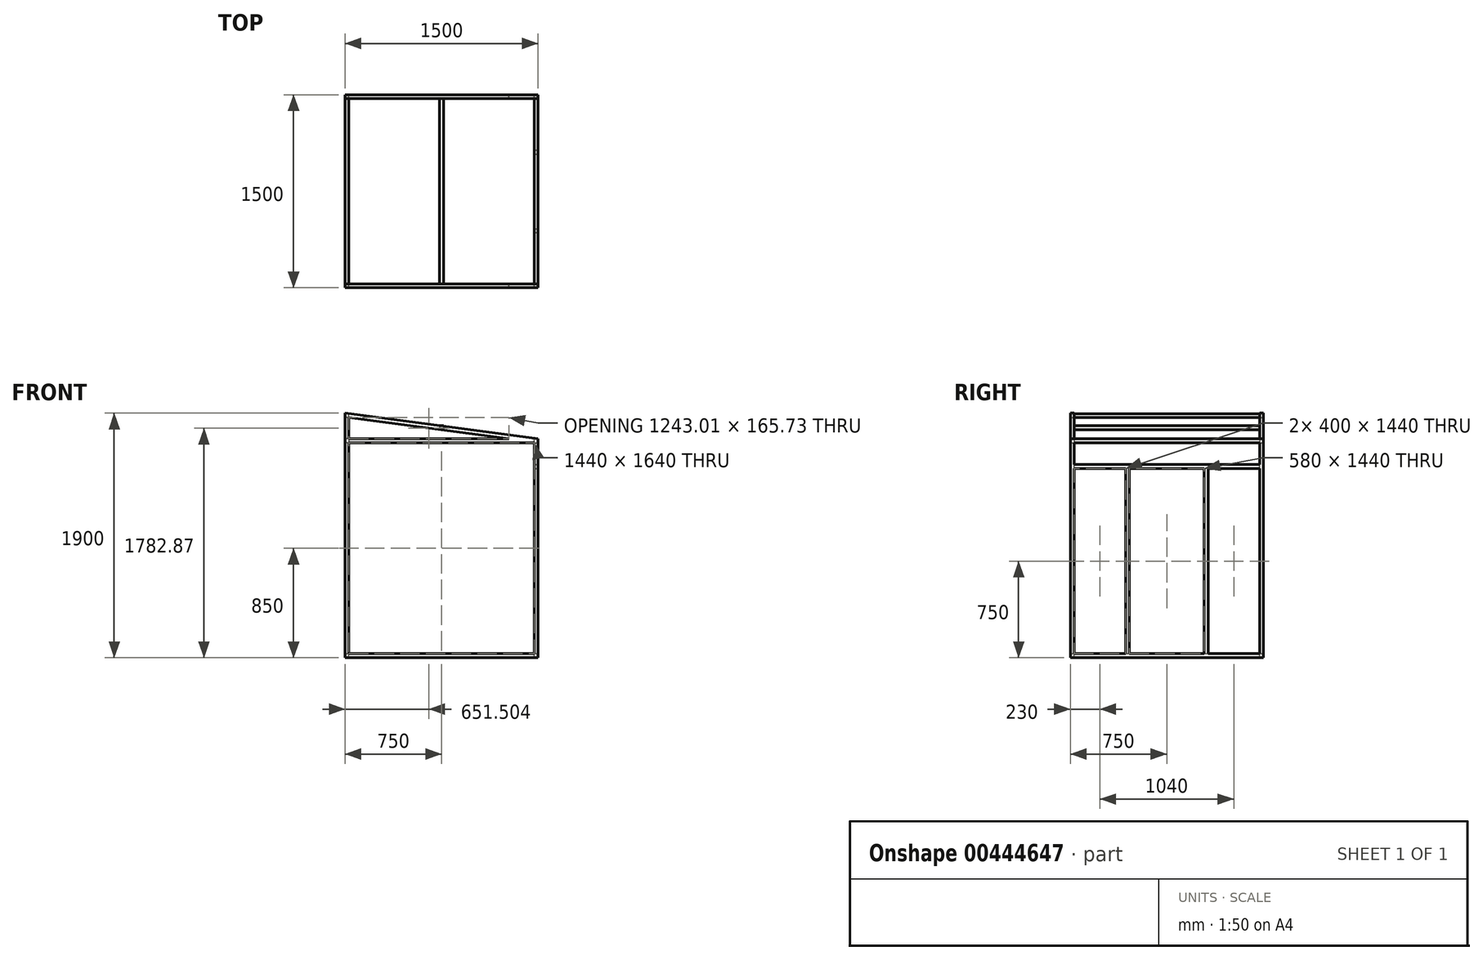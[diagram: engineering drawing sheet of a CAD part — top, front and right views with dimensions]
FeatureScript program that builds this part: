
annotation { "Feature Type Name" : "Feature", "Feature Type Description" : "" }
export const myFeature = defineFeature(function(context is Context, id is Id, definition is map)
    precondition{}
    {
        {
            var Q0;
            Q0=qCreatedBy(makeId("Front.planeOp"),FACE);
            var sketch = newSketch(context, id + "F0", { "sketchPlane" : qUnion([Q0])});
            skLineSegment(sketch, "E0.bottom", {"start": v(0, 0) * mm, "end": v(1500, 0) * mm});
            skLineSegment(sketch, "E0.top", {"start": v(30, 1700) * mm, "end": v(1500, 1700) * mm});
            skLineSegment(sketch, "E0.left", {"start": v(0, 0) * mm, "end": v(0, 1700) * mm});
            skLineSegment(sketch, "E0.right", {"start": v(1500, 0) * mm, "end": v(1500, 1700) * mm});
            skLineSegment(sketch, "E1.0", {"start": v(30, 30) * mm, "end": v(30, 1670) * mm});
            skLineSegment(sketch, "E1.1", {"start": v(30, 30) * mm, "end": v(1470, 30) * mm});
            skLineSegment(sketch, "E1.2", {"start": v(1470, 30) * mm, "end": v(1470, 1670) * mm});
            skLineSegment(sketch, "E1.3", {"start": v(30, 1670) * mm, "end": v(1470, 1670) * mm});
            skLineSegment(sketch, "E2", {"start": v(0, 1700) * mm, "end": v(0, 1900) * mm});
            skLineSegment(sketch, "E3", {"start": v(0, 1900) * mm, "end": v(1500, 1700) * mm});
            skLineSegment(sketch, "E4.0", {"start": v(30, 1865.73) * mm, "end": v(1496.04, 1670.26) * mm});
            skLineSegment(sketch, "E4.1", {"start": v(30, 1500) * mm, "end": v(30, 1865.73) * mm});
            skSolve(sketch);
        }
        {
            var Q0;
            Q0 = qSketchRegion(id + "F0", true);
            extrude(context, id + "F1", {"entities" : qUnion([Q0]), "depth" : 30 * mm});
        }
        {
            var Q0;
            Q0=makeQuery(id+"F1.opExtrude","CAP_FACE",FACE,{"disambiguationData":[OSD([sQuery(id+"F0.wireOp",EDGE,"E0.bottom"),sQuery(id+"F0.wireOp",EDGE,"E0.top"),sQuery(id+"F0.wireOp",EDGE,"E0.left"),sQuery(id+"F0.wireOp",EDGE,"E0.right"),sQuery(id+"F0.wireOp",EDGE,"E1.0"),sQuery(id+"F0.wireOp",EDGE,"E1.1"),sQuery(id+"F0.wireOp",EDGE,"E1.2"),sQuery(id+"F0.wireOp",EDGE,"E1.3")])],"isStart":false});
            var sketch = newSketch(context, id + "F2", { "sketchPlane" : qUnion([Q0])});
            skLineSegment(sketch, "E5.bottom", {"start": v(0, 0) * mm, "end": v(30, 0) * mm});
            skLineSegment(sketch, "E5.top", {"start": v(0, 30) * mm, "end": v(30, 30) * mm});
            skLineSegment(sketch, "E5.left", {"start": v(0, 0) * mm, "end": v(0, 30) * mm});
            skLineSegment(sketch, "E5.right", {"start": v(30, 0) * mm, "end": v(30, 30) * mm});
            skLineSegment(sketch, "E6.bottom", {"start": v(1500, 0) * mm, "end": v(1470, 0) * mm});
            skLineSegment(sketch, "E6.top", {"start": v(1500, 30) * mm, "end": v(1470, 30) * mm});
            skLineSegment(sketch, "E6.left", {"start": v(1500, 0) * mm, "end": v(1500, 30) * mm});
            skLineSegment(sketch, "E6.right", {"start": v(1470, 0) * mm, "end": v(1470, 30) * mm});
            skLineSegment(sketch, "E7.bottom", {"start": v(30, 1700) * mm, "end": v(0, 1700) * mm});
            skLineSegment(sketch, "E7.top", {"start": v(30, 30) * mm, "end": v(0, 30) * mm});
            skLineSegment(sketch, "E8.bottom", {"start": v(1470, 1670) * mm, "end": v(1500, 1670) * mm});
            skLineSegment(sketch, "E8.top", {"start": v(1470, 1700) * mm, "end": v(1500, 1700) * mm});
            skLineSegment(sketch, "E8.left", {"start": v(1470, 1670) * mm, "end": v(1470, 1700) * mm});
            skLineSegment(sketch, "E8.right", {"start": v(1500, 1670) * mm, "end": v(1500, 1700) * mm});
            skLineSegment(sketch, "E9.bottom", {"start": v(30, 1865.73) * mm, "end": v(0, 1865.73) * mm});
            skLineSegment(sketch, "E9.top", {"start": v(30, 1895.73) * mm, "end": v(0, 1895.73) * mm});
            skLineSegment(sketch, "E9.left", {"start": v(30, 1865.73) * mm, "end": v(30, 1895.73) * mm});
            skLineSegment(sketch, "E9.right", {"start": v(0, 1865.73) * mm, "end": v(0, 1895.73) * mm});
            skLineSegment(sketch, "E10.bottom", {"start": v(735, 1802) * mm, "end": v(765, 1802) * mm});
            skLineSegment(sketch, "E10.top", {"start": v(735, 1772) * mm, "end": v(765, 1772) * mm});
            skLineSegment(sketch, "E10.left", {"start": v(735, 1802) * mm, "end": v(735, 1772) * mm});
            skLineSegment(sketch, "E10.right", {"start": v(765, 1802) * mm, "end": v(765, 1772) * mm});
            skLineSegment(sketch, "E11", {"start": v(30, 1670) * mm, "end": v(0, 1670) * mm});
            skLineSegment(sketch, "E12", {"start": v(30, 1700) * mm, "end": v(30, 1670) * mm});
            skLineSegment(sketch, "E13.bottom", {"start": v(0, 1700) * mm, "end": v(30, 1700) * mm});
            skLineSegment(sketch, "E13.top", {"start": v(0, 1670) * mm, "end": v(30, 1670) * mm});
            skLineSegment(sketch, "E13.left", {"start": v(0, 1700) * mm, "end": v(0, 1670) * mm});
            skSolve(sketch);
        }
        {
            var Q0;
            Q0 = qSketchRegion(id + "F2", true);
            extrude(context, id + "F3", {"entities" : qUnion([Q0]), "operationType" : NewBodyOperationType.ADD, "depth" : 1440 * mm});
        }
        {
            var Q0;
            Q0=makeQuery(id+"F3.opExtrude","CAP_FACE",FACE,{"disambiguationData":[OSD([sQuery(id+"F2.wireOp",EDGE,"E5.bottom"),sQuery(id+"F2.wireOp",EDGE,"E5.top"),sQuery(id+"F2.wireOp",EDGE,"E5.left"),sQuery(id+"F2.wireOp",EDGE,"E5.right")])],"isStart":false});
            var sketch = newSketch(context, id + "F4", { "sketchPlane" : qUnion([Q0])});
            skLineSegment(sketch, "E14", {"start": v(0, 0) * mm, "end": v(0, 1900) * mm});
            skLineSegment(sketch, "E15", {"start": v(0, 1900) * mm, "end": v(1500, 1700) * mm});
            skLineSegment(sketch, "E16", {"start": v(1500, 1700) * mm, "end": v(1500, 0) * mm});
            skLineSegment(sketch, "E17", {"start": v(1500, 0) * mm, "end": v(0, 0) * mm});
            skLineSegment(sketch, "E18.0", {"start": v(30, 1865.73) * mm, "end": v(1273, 1700) * mm});
            skLineSegment(sketch, "E18.1", {"start": v(30, 30) * mm, "end": v(30, 1670) * mm});
            skLineSegment(sketch, "E18.2", {"start": v(1470, 30) * mm, "end": v(30, 30) * mm});
            skLineSegment(sketch, "E18.3", {"start": v(1470, 1673.73) * mm, "end": v(1470, 30) * mm});
            skLineSegment(sketch, "E19.bottom", {"start": v(30, 1670) * mm, "end": v(1500, 1670) * mm});
            skLineSegment(sketch, "E19.top", {"start": v(30, 1700) * mm, "end": v(1273, 1700) * mm});
            skLineSegment(sketch, "E19.right", {"start": v(1500, 1670) * mm, "end": v(1500, 1700) * mm});
            skLineSegment(sketch, "E20.trimOffspring", {"start": v(30, 1700) * mm, "end": v(30, 1865.73) * mm});
            skSolve(sketch);
        }
        {
            var Q0;
            Q0 = qSketchRegion(id + "F4", true);
            extrude(context, id + "F5", {"entities" : qUnion([Q0]), "operationType" : NewBodyOperationType.ADD, "depth" : 30 * mm});
        }
        {
            var Q0;
            Q0=makeQuery(id+"F5.boolean.opBoolean","MERGE",FACE,{"derivedFrom":[makeQuery(id+"F3.boolean.opBoolean","MERGE",FACE,{"derivedFrom":[makeQuery(id+"F1.opExtrude","SWEPT_FACE",FACE,{"disambiguationData":[OSD([sQuery(id+"F0.wireOp",EDGE,"E0.right")])]}),makeQuery(id+"F3.opExtrude","SWEPT_FACE",FACE,{"disambiguationData":[OSD([sQuery(id+"F2.wireOp",EDGE,"E6.left")])]}),makeQuery(id+"F3.opExtrude","SWEPT_FACE",FACE,{"disambiguationData":[OSD([sQuery(id+"F2.wireOp",EDGE,"E8.right")])]})]}),makeQuery(id+"F5.opExtrude","SWEPT_FACE",FACE,{"disambiguationData":[OSD([sQuery(id+"F4.wireOp",EDGE,"E16"),sQuery(id+"F4.wireOp",EDGE,"E19.right")])]})]});
            var sketch = newSketch(context, id + "F6", { "sketchPlane" : qUnion([Q0])});
            skLineSegment(sketch, "E21", {"start": v(-1070, 30) * mm, "end": v(-1070, 1470) * mm});
            skLineSegment(sketch, "E22", {"start": v(-1070, 1470) * mm, "end": v(-1470, 1470) * mm});
            skLineSegment(sketch, "E23", {"start": v(-1470, 1470) * mm, "end": v(-1470, 1500) * mm});
            skLineSegment(sketch, "E24", {"start": v(-1470, 1500) * mm, "end": v(-30, 1500) * mm});
            skLineSegment(sketch, "E25", {"start": v(-30, 1500) * mm, "end": v(-30, 1470) * mm});
            skLineSegment(sketch, "E26", {"start": v(-30, 1470) * mm, "end": v(-430, 1470) * mm});
            skLineSegment(sketch, "E27", {"start": v(-430, 1470) * mm, "end": v(-430, 30) * mm});
            skLineSegment(sketch, "E28", {"start": v(-430, 30) * mm, "end": v(-460, 30) * mm});
            skLineSegment(sketch, "E29", {"start": v(-460, 30) * mm, "end": v(-460, 1470) * mm});
            skLineSegment(sketch, "E30", {"start": v(-460, 1470) * mm, "end": v(-1040, 1470) * mm});
            skLineSegment(sketch, "E31", {"start": v(-1040, 1470) * mm, "end": v(-1040, 30) * mm});
            skLineSegment(sketch, "E32", {"start": v(-1040, 30) * mm, "end": v(-1070, 30) * mm});
            skSolve(sketch);
        }
        {
            var Q0;
            Q0 = qSketchRegion(id + "F6", true);
            extrude(context, id + "F7", {"entities" : qUnion([Q0]), "operationType" : NewBodyOperationType.ADD, "oppositeDirection" : true, "depth" : 30 * mm});
        }
    });
